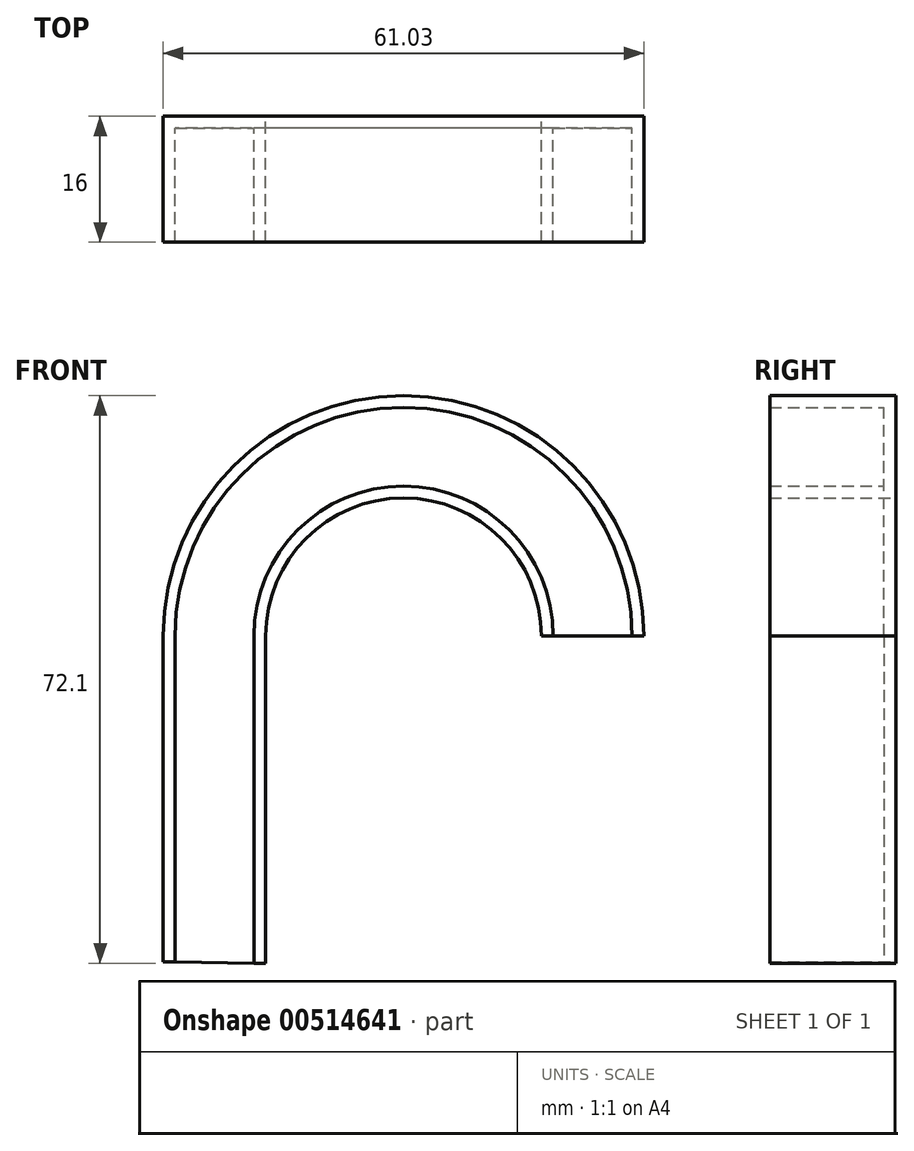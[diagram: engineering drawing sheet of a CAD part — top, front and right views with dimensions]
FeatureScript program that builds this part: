
annotation { "Feature Type Name" : "Feature", "Feature Type Description" : "" }
export const myFeature = defineFeature(function(context is Context, id is Id, definition is map)
    precondition{}
    {
        {
            var Q0;
            Q0=qCreatedBy(makeId("Front.planeOp"),FACE);
            var sketch = newSketch(context, id + "F0", { "sketchPlane" : qUnion([Q0])});
            skLineSegment(sketch, "E0.1", {"start": v(10, 36.71) * mm, "end": v(10, 36.71) * mm});
            skArc(sketch, "E1.0", {"start": v(45.03, 36.71) * mm, "mid": v(27.51, 54.22) * mm, "end": v(10, 36.71) * mm});
            skLineSegment(sketch, "E2", {"start": v(45.03, 36.71) * mm, "end": v(58.03, 36.71) * mm});
            skArc(sketch, "E3.0", {"start": v(58.03, 36.71) * mm, "mid": v(27.51, 67.22) * mm, "end": v(-3, 36.71) * mm});
            skLineSegment(sketch, "E4", {"start": v(10, 36.71) * mm, "end": v(10, -4.88) * mm});
            skLineSegment(sketch, "E5", {"start": v(-3, 36.71) * mm, "end": v(-3, -4.71) * mm});
            skLineSegment(sketch, "E6", {"start": v(-3, -4.71) * mm, "end": v(10, -4.88) * mm});
            skSolve(sketch);
        }
        {
            var Q0;
            Q0 = qSketchRegion(id + "F0", true);
            extrude(context, id + "F1", {"entities" : qUnion([Q0]), "depth" : 16 * mm, "offsetDistance" : 25 * mm});
        }
        {
            var Q0;
            Q0=makeQuery(id+"F1.opExtrude","CAP_FACE",FACE,{"disambiguationData":[OSD([sQuery(id+"F0.wireOp",EDGE,"E1.0"),sQuery(id+"F0.wireOp",EDGE,"E2"),sQuery(id+"F0.wireOp",EDGE,"E3.0"),sQuery(id+"F0.wireOp",EDGE,"E4"),sQuery(id+"F0.wireOp",EDGE,"E5"),sQuery(id+"F0.wireOp",EDGE,"E6")])],"isStart":false});
            var Q1;
            Q1=makeQuery(id+"F1.opExtrude","SWEPT_FACE",FACE,{"disambiguationData":[OSD([sQuery(id+"F0.wireOp",EDGE,"E6")])]});
            var Q2;
            Q2=makeQuery(id+"F1.opExtrude","SWEPT_FACE",FACE,{"disambiguationData":[OSD([sQuery(id+"F0.wireOp",EDGE,"E2")])]});
            shell(context, id + "F2", {"entities" : qUnion([Q0, Q1, Q2]), "thickness" : 1.5 * mm});
        }
    });
